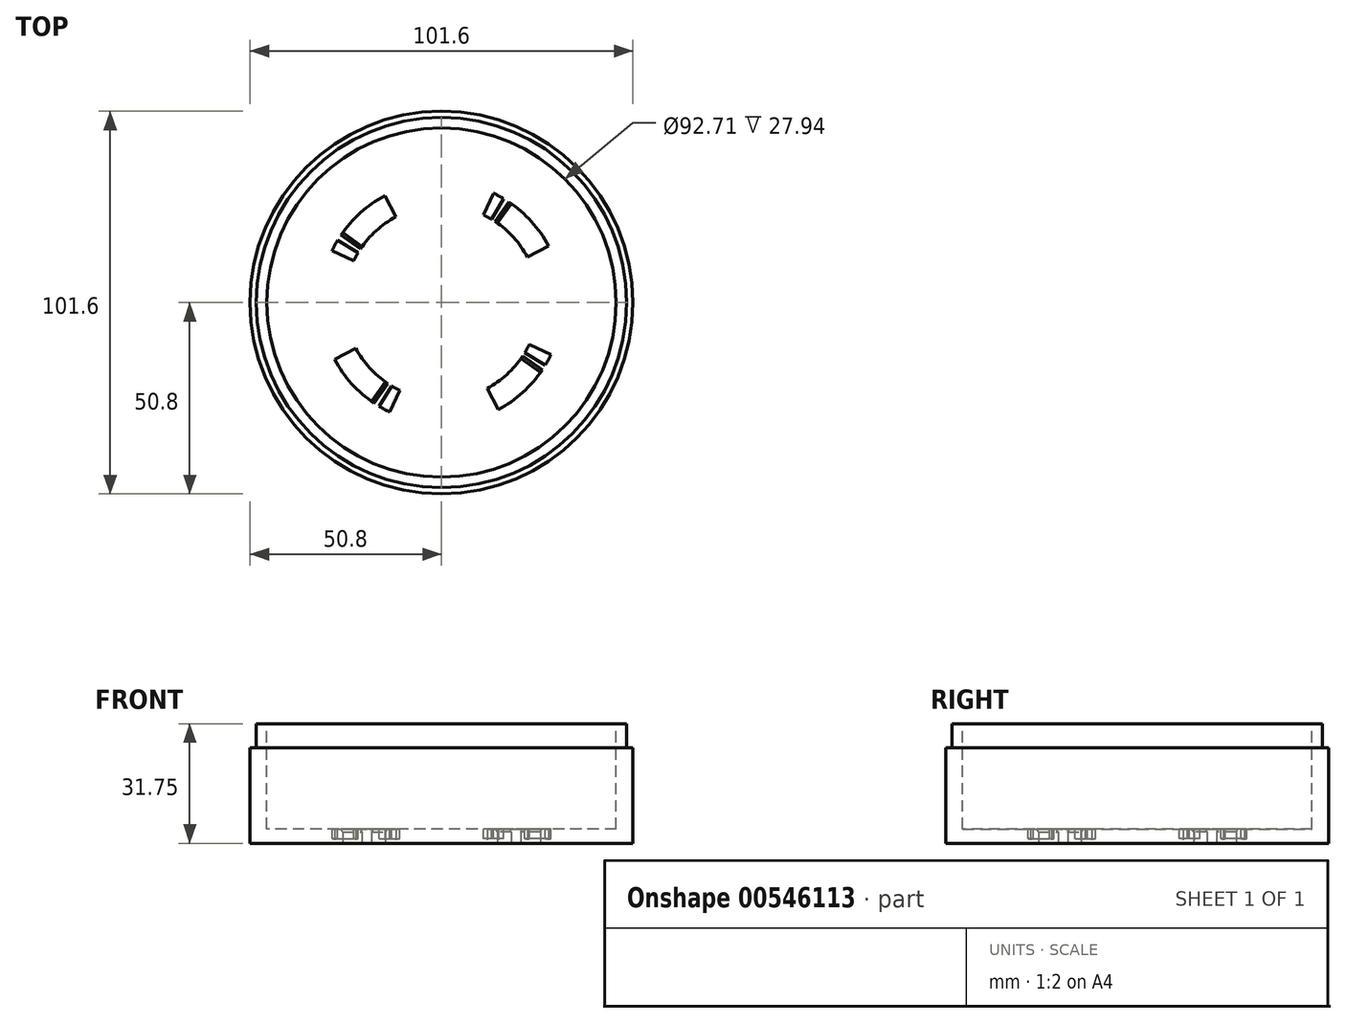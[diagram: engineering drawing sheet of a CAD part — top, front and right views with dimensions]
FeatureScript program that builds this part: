
annotation { "Feature Type Name" : "Feature", "Feature Type Description" : "" }
export const myFeature = defineFeature(function(context is Context, id is Id, definition is map)
    precondition{}
    {
        {
            var Q0;
            Q0=qCreatedBy(makeId("Top.planeOp"),FACE);
            var sketch = newSketch(context, id + "F0", { "sketchPlane" : qUnion([Q0])});
            skCircle(sketch, "E0", {"center": v(0, 0) * mm, "radius": 50.8 * mm});
            skSolve(sketch);
        }
        {
            var Q0;
            Q0 = qSketchRegion(id + "F0", true);
            extrude(context, id + "F1", {"entities" : qUnion([Q0]), "depth" : 25.4 * mm, "offsetDistance" : 25.4 * mm});
        }
        {
            var Q0;
            Q0=makeQuery(id+"F1.opExtrude","CAP_FACE",FACE,{"disambiguationData":[OSD([sQuery(id+"F0.wireOp",EDGE,"E0")])],"isStart":false});
            var sketch = newSketch(context, id + "F2", { "sketchPlane" : qUnion([Q0])});
            skCircle(sketch, "E1", {"center": v(0, 0) * mm, "radius": 49.15 * mm});
            skSolve(sketch);
        }
        {
            var Q0;
            Q0 = qSketchRegion(id + "F2", true);
            extrude(context, id + "F3", {"entities" : qUnion([Q0]), "operationType" : NewBodyOperationType.ADD, "depth" : 6.35 * mm, "offsetDistance" : 25.4 * mm});
        }
        {
            var Q0;
            Q0=makeQuery(id+"F3.opExtrude","CAP_FACE",FACE,{"disambiguationData":[OSD([sQuery(id+"F2.wireOp",EDGE,"E1")])],"isStart":false});
            var sketch = newSketch(context, id + "F4", { "sketchPlane" : qUnion([Q0])});
            skCircle(sketch, "E2", {"center": v(0, 0) * mm, "radius": 46.35 * mm});
            skSolve(sketch);
        }
        {
            var Q0;
            Q0 = qSketchRegion(id + "F4", true);
            extrude(context, id + "F5", {"entities" : qUnion([Q0]), "operationType" : NewBodyOperationType.REMOVE, "oppositeDirection" : true, "depth" : 27.94 * mm, "offsetDistance" : 25.4 * mm});
        }
        {
            var Q0;
            Q0=makeQuery(id+"F1.opExtrude","CAP_FACE",FACE,{"disambiguationData":[OSD([sQuery(id+"F0.wireOp",EDGE,"E0")])],"isStart":true});
            var sketch = newSketch(context, id + "F6", { "sketchPlane" : qUnion([Q0])});
            skArc(sketch, "E3", {"start": v(15.08, 28.39) * mm, "mid": v(21.25, 24.12) * mm, "end": v(26.26, 18.53) * mm});
            skArc(sketch, "E4.0", {"start": v(12.1, 22.78) * mm, "mid": v(17.05, 19.35) * mm, "end": v(21.08, 14.87) * mm});
            skLineSegment(sketch, "E5", {"start": v(21.08, 14.87) * mm, "end": v(26.26, 18.53) * mm});
            skLineSegment(sketch, "E6", {"start": v(12.1, 22.78) * mm, "end": v(15.08, 28.39) * mm});
            skArc(sketch, "E7.1.0", {"start": v(-28.39, 15.08) * mm, "mid": v(-24.12, 21.25) * mm, "end": v(-18.53, 26.26) * mm});
            skLineSegment(sketch, "E7.1.1", {"start": v(-14.87, 21.08) * mm, "end": v(-18.53, 26.26) * mm});
            skArc(sketch, "E7.1.2", {"start": v(-22.78, 12.1) * mm, "mid": v(-19.35, 17.05) * mm, "end": v(-14.87, 21.08) * mm});
            skLineSegment(sketch, "E7.1.3", {"start": v(-22.78, 12.1) * mm, "end": v(-28.39, 15.08) * mm});
            skArc(sketch, "E7.2.0", {"start": v(-15.08, -28.39) * mm, "mid": v(-21.25, -24.12) * mm, "end": v(-26.26, -18.53) * mm});
            skLineSegment(sketch, "E7.2.1", {"start": v(-21.08, -14.87) * mm, "end": v(-26.26, -18.53) * mm});
            skArc(sketch, "E7.2.2", {"start": v(-12.1, -22.78) * mm, "mid": v(-17.05, -19.35) * mm, "end": v(-21.08, -14.87) * mm});
            skLineSegment(sketch, "E7.2.3", {"start": v(-12.1, -22.78) * mm, "end": v(-15.08, -28.39) * mm});
            skArc(sketch, "E7.3.0", {"start": v(28.39, -15.08) * mm, "mid": v(24.12, -21.25) * mm, "end": v(18.53, -26.26) * mm});
            skLineSegment(sketch, "E7.3.1", {"start": v(14.87, -21.08) * mm, "end": v(18.53, -26.26) * mm});
            skArc(sketch, "E7.3.2", {"start": v(22.78, -12.1) * mm, "mid": v(19.35, -17.05) * mm, "end": v(14.87, -21.08) * mm});
            skLineSegment(sketch, "E7.3.3", {"start": v(22.78, -12.1) * mm, "end": v(28.39, -15.08) * mm});
            skSolve(sketch);
        }
        {
            var Q0;
            Q0 = qSketchRegion(id + "F6", true);
            extrude(context, id + "F7", {"entities" : qUnion([Q0]), "operationType" : NewBodyOperationType.REMOVE, "endBound" : BoundingType.THROUGH_ALL, "oppositeDirection" : true, "depth" : 25.4 * mm, "offsetDistance" : 25.4 * mm});
        }
        {
            var Q0;
            Q0=makeQuery(id+"F5.boolean.opBoolean","COPY",FACE,{"derivedFrom":makeQuery(id+"F5.opExtrude","CAP_FACE",FACE,{"disambiguationData":[OSD([sQuery(id+"F4.wireOp",EDGE,"E2")])],"isStart":false})});
            var sketch = newSketch(context, id + "F8", { "sketchPlane" : qUnion([Q0])});
            skArc(sketch, "E8", {"start": v(-27.56, 16.53) * mm, "mid": v(-28.33, 15.18) * mm, "end": v(-29.03, 13.8) * mm});
            skArc(sketch, "E9.0", {"start": v(-22.12, 13.27) * mm, "mid": v(-22.73, 12.18) * mm, "end": v(-23.3, 11.07) * mm});
            skLineSegment(sketch, "E10", {"start": v(-27.56, 16.53) * mm, "end": v(-22.12, 13.27) * mm});
            skLineSegment(sketch, "E11", {"start": v(-29.03, 13.8) * mm, "end": v(-23.3, 11.07) * mm});
            skLineSegment(sketch, "E12.1.0", {"start": v(-16.53, -27.56) * mm, "end": v(-13.27, -22.12) * mm});
            skArc(sketch, "E12.1.1", {"start": v(-16.53, -27.56) * mm, "mid": v(-15.18, -28.33) * mm, "end": v(-13.8, -29.03) * mm});
            skLineSegment(sketch, "E12.1.2", {"start": v(-13.8, -29.03) * mm, "end": v(-11.07, -23.3) * mm});
            skArc(sketch, "E12.1.3", {"start": v(-13.27, -22.12) * mm, "mid": v(-12.18, -22.73) * mm, "end": v(-11.07, -23.3) * mm});
            skLineSegment(sketch, "E12.2.0", {"start": v(27.56, -16.53) * mm, "end": v(22.12, -13.27) * mm});
            skArc(sketch, "E12.2.1", {"start": v(27.56, -16.53) * mm, "mid": v(28.33, -15.18) * mm, "end": v(29.03, -13.8) * mm});
            skLineSegment(sketch, "E12.2.2", {"start": v(29.03, -13.8) * mm, "end": v(23.3, -11.07) * mm});
            skArc(sketch, "E12.2.3", {"start": v(22.12, -13.27) * mm, "mid": v(22.73, -12.18) * mm, "end": v(23.3, -11.07) * mm});
            skLineSegment(sketch, "E12.3.0", {"start": v(16.53, 27.56) * mm, "end": v(13.27, 22.12) * mm});
            skArc(sketch, "E12.3.1", {"start": v(16.53, 27.56) * mm, "mid": v(15.18, 28.33) * mm, "end": v(13.8, 29.03) * mm});
            skLineSegment(sketch, "E12.3.2", {"start": v(13.8, 29.03) * mm, "end": v(11.07, 23.3) * mm});
            skArc(sketch, "E12.3.3", {"start": v(13.27, 22.12) * mm, "mid": v(12.18, 22.73) * mm, "end": v(11.07, 23.3) * mm});
            skSolve(sketch);
        }
        {
            var Q0;
            Q0 = qSketchRegion(id + "F8", true);
            extrude(context, id + "F9", {"entities" : qUnion([Q0]), "operationType" : NewBodyOperationType.REMOVE, "oppositeDirection" : true, "depth" : 2.54 * mm, "offsetDistance" : 25.4 * mm});
        }
        {
            var Q0;
            Q0=makeQuery(id+"F7.boolean.opBoolean","INTERSECT",EDGE,{"derivedFrom":[makeQuery(id+"F5.boolean.opBoolean","COPY",FACE,{"derivedFrom":makeQuery(id+"F5.opExtrude","CAP_FACE",FACE,{"disambiguationData":[OSD([sQuery(id+"F4.wireOp",EDGE,"E2")])],"isStart":false})}),makeQuery(id+"F7.opExtrude","SWEPT_FACE",FACE,{"disambiguationData":[OSD([sQuery(id+"F6.wireOp",EDGE,"E7.2.1")])]})]});
            var Q1;
            Q1=makeQuery(id+"F9.boolean.opBoolean","COPY",EDGE,{"derivedFrom":makeQuery(id+"F9.opExtrude","CAP_EDGE",EDGE,{"disambiguationData":[OSD([sQuery(id+"F8.wireOp",EDGE,"E10")])],"isStart":true})});
            var Q2;
            Q2=makeQuery(id+"F9.boolean.opBoolean","COPY",EDGE,{"derivedFrom":makeQuery(id+"F9.opExtrude","CAP_EDGE",EDGE,{"disambiguationData":[OSD([sQuery(id+"F8.wireOp",EDGE,"E12.3.2")])],"isStart":true})});
            var Q3;
            Q3=makeQuery(id+"F9.boolean.opBoolean","COPY",EDGE,{"derivedFrom":makeQuery(id+"F9.opExtrude","CAP_EDGE",EDGE,{"disambiguationData":[OSD([sQuery(id+"F8.wireOp",EDGE,"E12.3.0")])],"isStart":true})});
            var Q4;
            Q4=makeQuery(id+"F9.boolean.opBoolean","COPY",EDGE,{"derivedFrom":makeQuery(id+"F9.opExtrude","CAP_EDGE",EDGE,{"disambiguationData":[OSD([sQuery(id+"F8.wireOp",EDGE,"E12.2.0")])],"isStart":true})});
            var Q5;
            Q5=makeQuery(id+"F9.boolean.opBoolean","COPY",EDGE,{"derivedFrom":makeQuery(id+"F9.opExtrude","CAP_EDGE",EDGE,{"disambiguationData":[OSD([sQuery(id+"F8.wireOp",EDGE,"E12.2.2")])],"isStart":true})});
            var Q6;
            Q6=makeQuery(id+"F9.boolean.opBoolean","COPY",EDGE,{"derivedFrom":makeQuery(id+"F9.opExtrude","CAP_EDGE",EDGE,{"disambiguationData":[OSD([sQuery(id+"F8.wireOp",EDGE,"E12.1.2")])],"isStart":true})});
            var Q7;
            Q7=makeQuery(id+"F9.boolean.opBoolean","COPY",EDGE,{"derivedFrom":makeQuery(id+"F9.opExtrude","CAP_EDGE",EDGE,{"disambiguationData":[OSD([sQuery(id+"F8.wireOp",EDGE,"E12.1.0")])],"isStart":true})});
            var Q8;
            Q8=makeQuery(id+"F7.boolean.opBoolean","INTERSECT",EDGE,{"derivedFrom":[makeQuery(id+"F5.boolean.opBoolean","COPY",FACE,{"derivedFrom":makeQuery(id+"F5.opExtrude","CAP_FACE",FACE,{"disambiguationData":[OSD([sQuery(id+"F4.wireOp",EDGE,"E2")])],"isStart":false})}),makeQuery(id+"F7.opExtrude","SWEPT_FACE",FACE,{"disambiguationData":[OSD([sQuery(id+"F6.wireOp",EDGE,"E5")])]})]});
            var Q9;
            Q9=makeQuery(id+"F7.boolean.opBoolean","INTERSECT",EDGE,{"derivedFrom":[makeQuery(id+"F5.boolean.opBoolean","COPY",FACE,{"derivedFrom":makeQuery(id+"F5.opExtrude","CAP_FACE",FACE,{"disambiguationData":[OSD([sQuery(id+"F4.wireOp",EDGE,"E2")])],"isStart":false})}),makeQuery(id+"F7.opExtrude","SWEPT_FACE",FACE,{"disambiguationData":[OSD([sQuery(id+"F6.wireOp",EDGE,"E7.3.1")])]})]});
            var Q10;
            Q10=makeQuery(id+"F7.boolean.opBoolean","INTERSECT",EDGE,{"derivedFrom":[makeQuery(id+"F5.boolean.opBoolean","COPY",FACE,{"derivedFrom":makeQuery(id+"F5.opExtrude","CAP_FACE",FACE,{"disambiguationData":[OSD([sQuery(id+"F4.wireOp",EDGE,"E2")])],"isStart":false})}),makeQuery(id+"F7.opExtrude","SWEPT_FACE",FACE,{"disambiguationData":[OSD([sQuery(id+"F6.wireOp",EDGE,"E7.1.1")])]})]});
            chamfer(context, id + "F10", {"entities" : qUnion([Q0, Q1, Q2, Q3, Q4, Q5, Q6, Q7, Q8, Q9, Q10]), "width" : 0.76 * mm, "tangentPropagation" : true});
        }
    });
